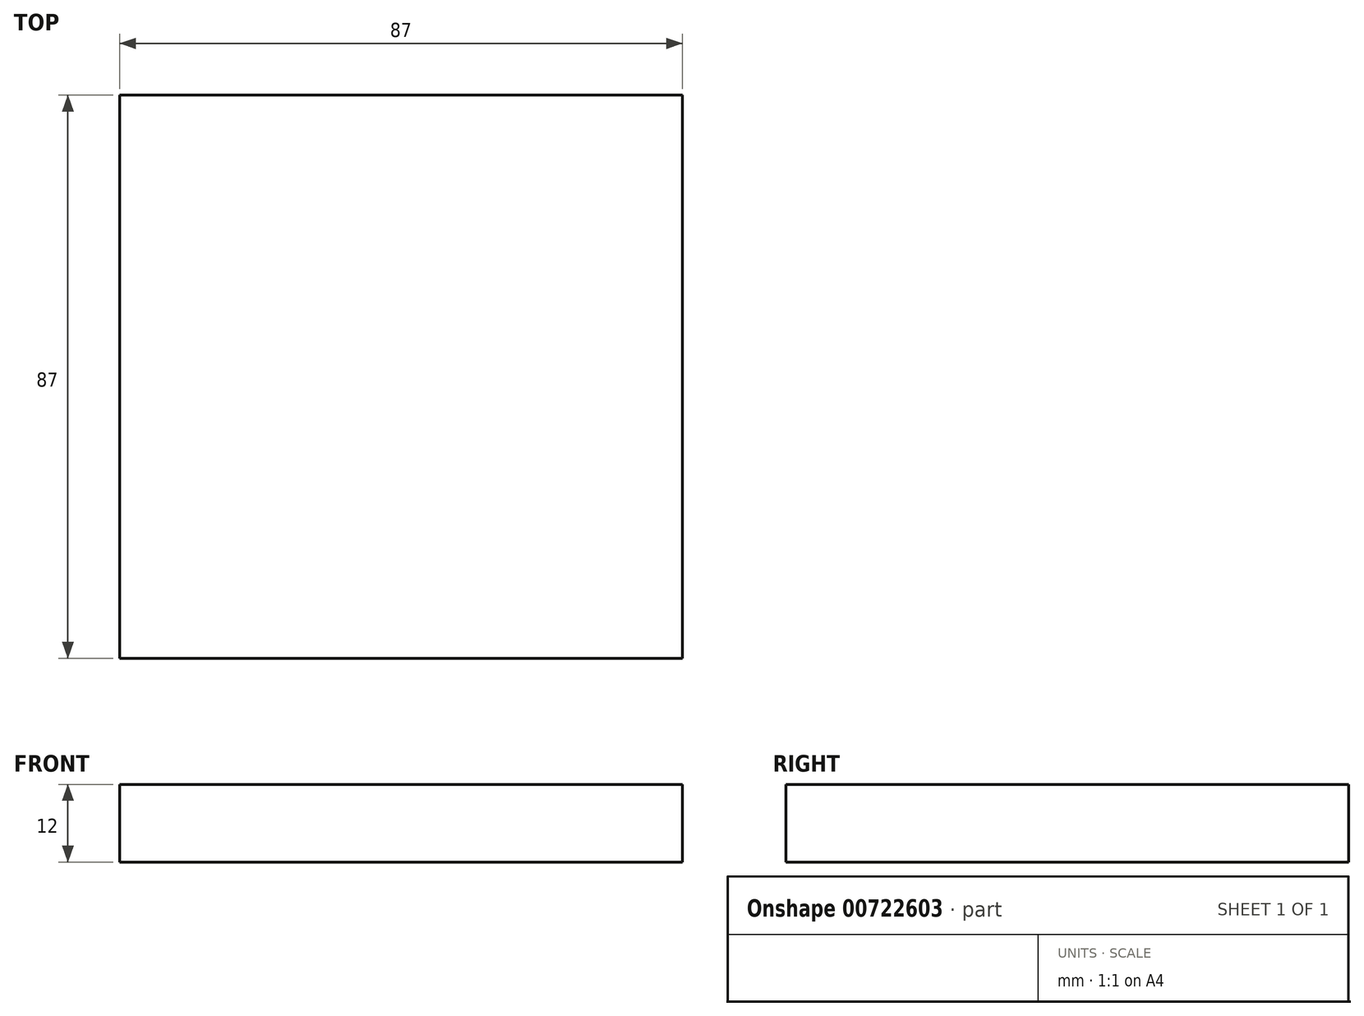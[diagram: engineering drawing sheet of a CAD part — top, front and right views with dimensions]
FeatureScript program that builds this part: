
annotation { "Feature Type Name" : "Feature", "Feature Type Description" : "" }
export const myFeature = defineFeature(function(context is Context, id is Id, definition is map)
    precondition{}
    {
        {
            var Q0;
            Q0=qCreatedBy(makeId("Front.planeOp"),FACE);
            var sketch = newSketch(context, id + "F0", { "sketchPlane" : qUnion([Q0])});
            skLineSegment(sketch, "E0.bottom", {"start": v(-43.5, 6) * mm, "end": v(43.5, 6) * mm});
            skLineSegment(sketch, "E0.top", {"start": v(-43.5, -6) * mm, "end": v(43.5, -6) * mm});
            skLineSegment(sketch, "E0.left", {"start": v(-43.5, 6) * mm, "end": v(-43.5, -6) * mm});
            skLineSegment(sketch, "E0.right", {"start": v(43.5, 6) * mm, "end": v(43.5, -6) * mm});
            skPoint(sketch, "E0.middle", {"position": v(0, 0) * mm});
            skSolve(sketch);
        }
        {
            var Q0;
            Q0=makeQuery(id+"F0.imprint","IMPRINT",FACE,{"disambiguationData":[TD([[makeQuery(id+"F0.imprint","IMPRINT",EDGE,{"derivedFrom":sQuery(id+"F0.wireOp",EDGE,"E0.bottom")}),-1.0]])]});
            extrude(context, id + "F1", {"entities" : qUnion([Q0]), "endBound" : BoundingType.SYMMETRIC, "depth" : 87 * mm, "offsetDistance" : 25 * mm});
        }
    });
